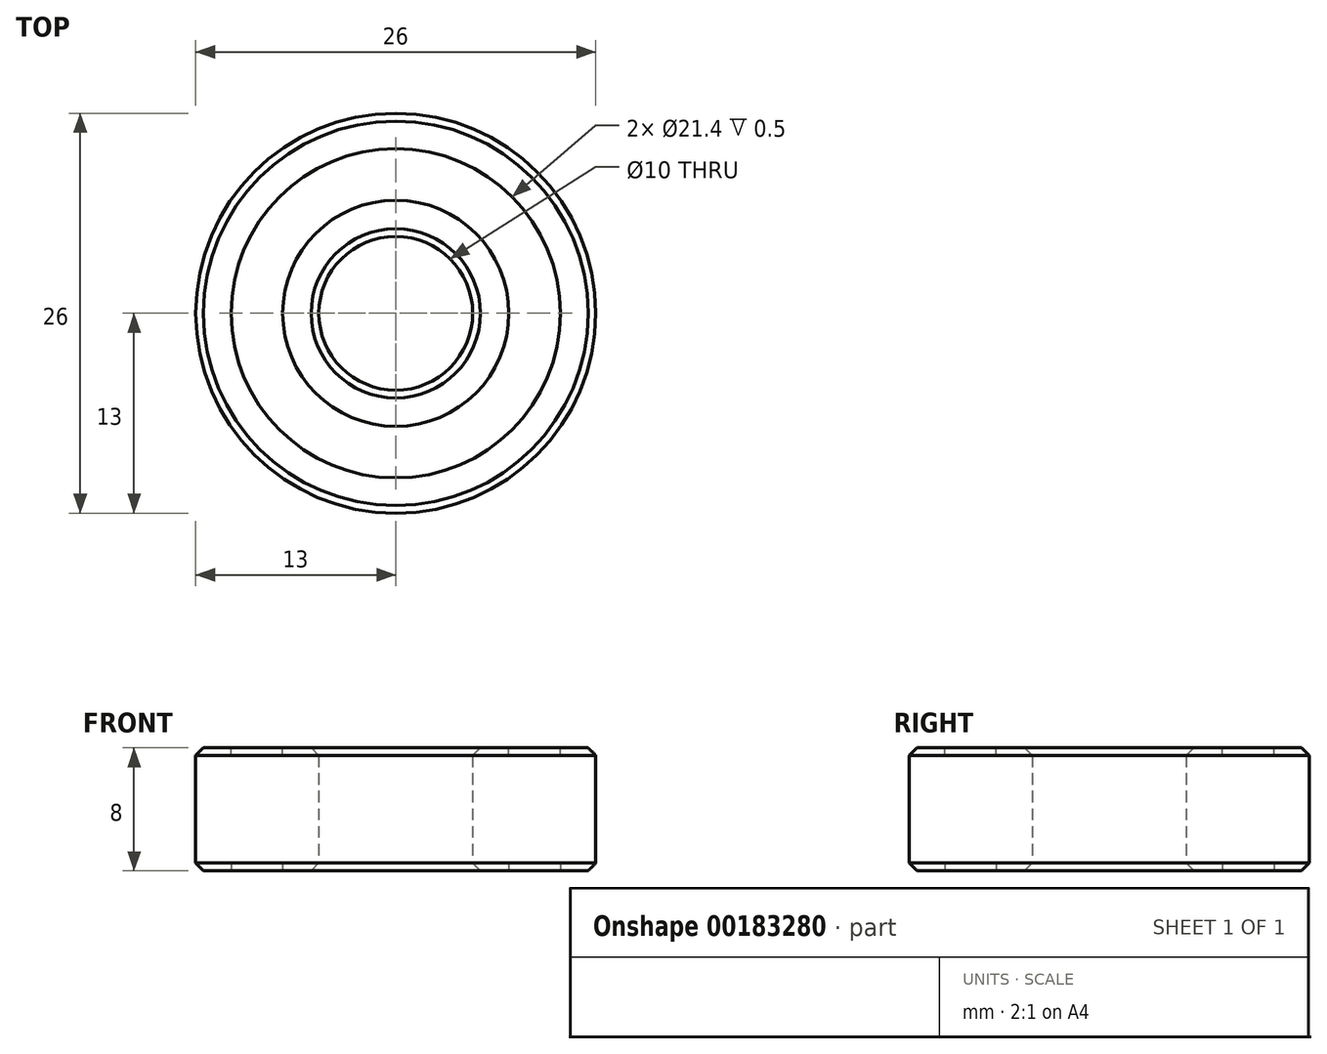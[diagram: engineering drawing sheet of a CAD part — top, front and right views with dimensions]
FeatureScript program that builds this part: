
annotation { "Feature Type Name" : "Feature", "Feature Type Description" : "" }
export const myFeature = defineFeature(function(context is Context, id is Id, definition is map)
    precondition{}
    {
        {
            var Q0;
            Q0=qCreatedBy(makeId("Top.planeOp"),FACE);
            var sketch = newSketch(context, id + "F0", { "sketchPlane" : qUnion([Q0])});
            skCircle(sketch, "E0", {"center": v(0, 0) * mm, "radius": 13 * mm});
            skCircle(sketch, "E1", {"center": v(0, 0) * mm, "radius": 5 * mm});
            skSolve(sketch);
        }
        {
            var Q0;
            Q0 = qSketchRegion(id + "F0", true);
            extrude(context, id + "F1", {"entities" : qUnion([Q0]), "endBound" : BoundingType.SYMMETRIC, "depth" : 8 * mm});
        }
        {
            var Q0;
            Q0=makeQuery(id+"F1.opExtrude","CAP_FACE",FACE,{"disambiguationData":[OSD([sQuery(id+"F0.wireOp",EDGE,"E0"),sQuery(id+"F0.wireOp",EDGE,"E1")])],"isStart":false});
            var sketch = newSketch(context, id + "F2", { "sketchPlane" : qUnion([Q0])});
            skCircle(sketch, "E2", {"center": v(0, 0) * mm, "radius": 7.35 * mm});
            skCircle(sketch, "E3", {"center": v(0, 0) * mm, "radius": 10.7 * mm});
            skSolve(sketch);
        }
        {
            var Q0;
            Q0 = qSketchRegion(id + "F2", true);
            extrude(context, id + "F3", {"entities" : qUnion([Q0]), "operationType" : NewBodyOperationType.REMOVE, "oppositeDirection" : true, "depth" : 0.5 * mm});
        }
        {
            var Q0;
            Q0=makeQuery(id+"F1.opExtrude","CAP_FACE",FACE,{"disambiguationData":[OSD([sQuery(id+"F0.wireOp",EDGE,"E0"),sQuery(id+"F0.wireOp",EDGE,"E1")])],"isStart":true});
            var sketch = newSketch(context, id + "F4", { "sketchPlane" : qUnion([Q0])});
            skCircle(sketch, "E4.0", {"center": v(0, 0) * mm, "radius": 10.7 * mm});
            skCircle(sketch, "E5.0", {"center": v(0, 0) * mm, "radius": 7.35 * mm});
            skSolve(sketch);
        }
        {
            var Q0;
            Q0 = qSketchRegion(id + "F4", true);
            extrude(context, id + "F5", {"entities" : qUnion([Q0]), "operationType" : NewBodyOperationType.REMOVE, "oppositeDirection" : true, "depth" : 0.5 * mm});
        }
        {
            var Q0;
            Q0=makeQuery(id+"F1.opExtrude","CAP_EDGE",EDGE,{"disambiguationData":[OSD([sQuery(id+"F0.wireOp",EDGE,"E0")])],"isStart":true});
            var Q1;
            Q1=makeQuery(id+"F1.opExtrude","CAP_EDGE",EDGE,{"disambiguationData":[OSD([sQuery(id+"F0.wireOp",EDGE,"E0")])],"isStart":false});
            var Q2;
            Q2=makeQuery(id+"F1.opExtrude","CAP_EDGE",EDGE,{"disambiguationData":[OSD([sQuery(id+"F0.wireOp",EDGE,"E1")])],"isStart":true});
            var Q3;
            Q3=makeQuery(id+"F1.opExtrude","CAP_EDGE",EDGE,{"disambiguationData":[OSD([sQuery(id+"F0.wireOp",EDGE,"E1")])],"isStart":false});
            chamfer(context, id + "F6", {"entities" : qUnion([Q0, Q1, Q2, Q3]), "width" : 0.5 * mm, "tangentPropagation" : true});
        }
    });
